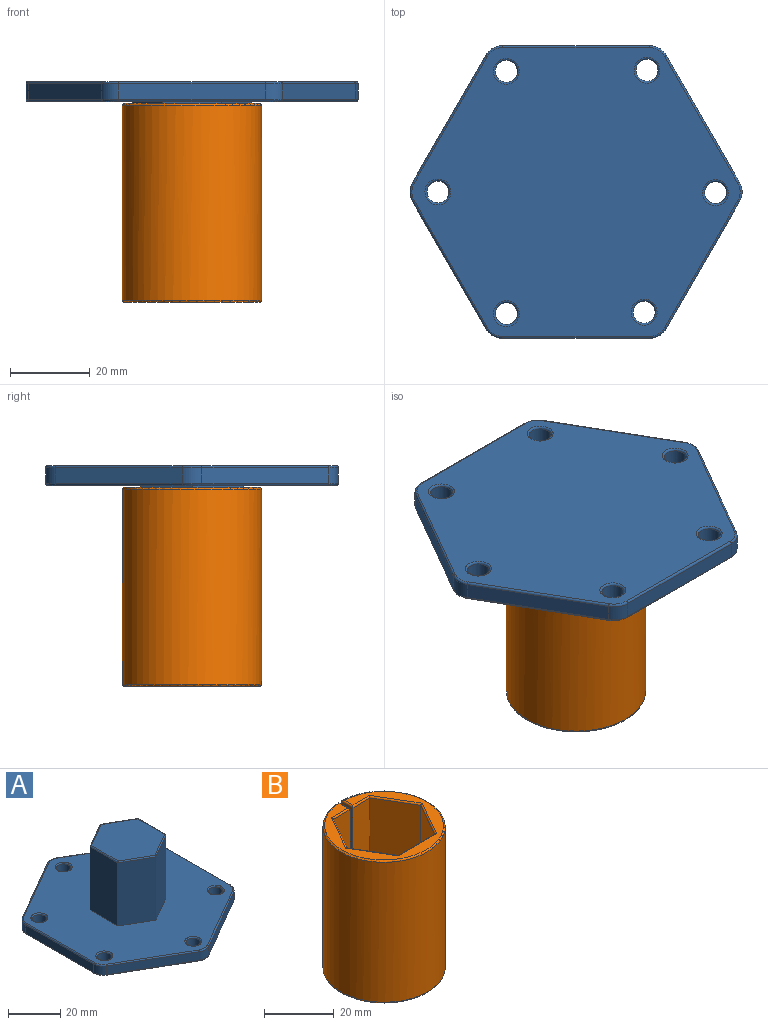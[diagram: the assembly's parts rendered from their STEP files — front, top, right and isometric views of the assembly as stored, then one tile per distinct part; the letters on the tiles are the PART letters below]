
ASSEMBLY  parts=2 mates=1
PART A: 69 faces, bbox 74.4x84.3x35 mm
  f0: plane 31.81x18.36mm, normal (0.5,0.87,0), area 146.9mm2, adj f27,f32,f33,f45
  f1: plane 31.81x18.36mm, normal (-0.5,0.87,0), area 146.9mm2, adj f27,f28,f36,f48
  f2: plane 36.73x4mm, normal (-1,0,0), area 146.9mm2, adj f28,f29,f40,f52
  f3: plane 31.81x18.36mm, normal (-0.5,-0.87,0), area 146.9mm2, adj f29,f30,f44,f56
  f4: plane 31.81x18.36mm, normal (0.5,-0.87,0), area 146.9mm2, adj f30,f31,f41,f53
  f5: cylinder r=2.75mm len=5.5mm, axis (0,0,-1), area 69.1mm2, adj f57,f63
  f6: cylinder r=2.75mm len=5.5mm, axis (0,0,-1), area 69.1mm2, adj f62,f68
  f7: cylinder r=2.75mm len=5.5mm, axis (0,0,-1), area 69.1mm2, adj f61,f67
  f8: cylinder r=2.75mm len=5.5mm, axis (0,0,-1), area 69.1mm2, adj f60,f66
  f9: cylinder r=2.75mm len=5.5mm, axis (0,0,-1), area 69.1mm2, adj f59,f65
  f10: cylinder r=2.75mm len=5.5mm, axis (0,0,-1), area 69.1mm2, adj f58,f64
  f11: plane 36.73x4mm, normal (1,0,0), area 146.9mm2, adj f31,f32,f37,f49
  f12: plane 82.45x72.61mm, normal (0,0,1), area 3775.9mm2, adj f14,f15,f16,f17,f18,f19,f33,f34
  f13: plane 82.45x72.61mm, normal (0,0,-1), area 4360.5mm2, adj f45,f46,f47,f48,f49,f50,f51,f52
  f14: plane 29.5x15mm, normal (1,0,0), area 442.5mm2, adj f12,f15,f19,f23
  f15: plane 29.5x12.99mm, normal (0.5,0.87,0), area 442.5mm2, adj f12,f14,f16,f21
  f16: plane 29.5x12.99mm, normal (-0.5,0.87,0), area 442.5mm2, adj f12,f15,f17,f22
  f17: plane 29.5x15mm, normal (-1,0,0), area 442.5mm2, adj f12,f16,f18,f24
  f18: plane 29.5x12.99mm, normal (-0.5,-0.87,0), area 442.5mm2, adj f12,f17,f19,f26
  f19: plane 29.5x12.99mm, normal (0.5,-0.87,0), area 442.5mm2, adj f12,f14,f18,f25
  f20: plane 28.85x24.98mm, normal (0,0,1), area 540.4mm2, adj f21,f22,f23,f24,f25,f26
  f21: cylinder r=0.5mm len=13.24mm, axis (0.87,-0.5,0), area 11.6mm2, adj f15,f20,f22,f23
  f22: cylinder r=0.5mm len=13.24mm, axis (0.87,0.5,0), area 11.6mm2, adj f16,f20,f21,f24
  f23: cylinder r=0.5mm len=15mm, axis (0,-1,0), area 11.6mm2, adj f14,f20,f21,f25
  f24: cylinder r=0.5mm len=15mm, axis (0,1,0), area 11.6mm2, adj f17,f20,f22,f26
  f25: cylinder r=0.5mm len=13.24mm, axis (-0.87,-0.5,0), area 11.6mm2, adj f19,f20,f23,f26
  f26: cylinder r=0.5mm len=13.24mm, axis (-0.87,0.5,0), area 11.6mm2, adj f18,f20,f24,f25
  f27: cylinder r=5mm len=5mm, axis (0,0,-1), area 20.9mm2, adj f0,f1,f34,f46
  f28: cylinder r=5mm len=4.33mm, axis (0,0,-1), area 20.9mm2, adj f1,f2,f38,f50
  f29: cylinder r=5mm len=4.33mm, axis (0,0,-1), area 20.9mm2, adj f2,f3,f42,f54
  f30: cylinder r=5mm len=5mm, axis (0,0,-1), area 20.9mm2, adj f3,f4,f43,f55
  f31: cylinder r=5mm len=4.33mm, axis (0,0,-1), area 20.9mm2, adj f4,f11,f39,f51
  f32: cylinder r=5mm len=4.33mm, axis (0,0,-1), area 20.9mm2, adj f0,f11,f35,f47
  f33: cylinder r=0.5mm len=32.06mm, axis (0.87,-0.5,0), area 28.8mm2, adj f0,f12,f34,f35
  f34: torus R=4.5mm, axis (0,0,1), area 4mm2, adj f12,f27,f33,f36
  f35: torus R=4.5mm, axis (0,0,1), area 4mm2, adj f12,f32,f33,f37
  f36: cylinder r=0.5mm len=32.06mm, axis (0.87,0.5,0), area 28.8mm2, adj f1,f12,f34,f38
  f37: cylinder r=0.5mm len=36.73mm, axis (0,-1,0), area 28.8mm2, adj f11,f12,f35,f39
  f38: torus R=4.5mm, axis (0,0,1), area 4mm2, adj f12,f28,f36,f40
  f39: torus R=4.5mm, axis (0,0,1), area 4mm2, adj f12,f31,f37,f41
  f40: cylinder r=0.5mm len=36.73mm, axis (0,1,0), area 28.8mm2, adj f2,f12,f38,f42
  f41: cylinder r=0.5mm len=32.06mm, axis (-0.87,-0.5,0), area 28.8mm2, adj f4,f12,f39,f43
  f42: torus R=4.5mm, axis (0,0,1), area 4mm2, adj f12,f29,f40,f44
  f43: torus R=4.5mm, axis (0,0,1), area 4mm2, adj f12,f30,f41,f44
  f44: cylinder r=0.5mm len=32.06mm, axis (-0.87,0.5,0), area 28.8mm2, adj f3,f12,f42,f43
  f45: cylinder r=0.5mm len=32.06mm, axis (-0.87,0.5,0), area 28.8mm2, adj f0,f13,f46,f47
  f46: torus R=4.5mm, axis (0,0,1), area 4mm2, adj f13,f27,f45,f48
  f47: torus R=4.5mm, axis (0,0,1), area 4mm2, adj f13,f32,f45,f49
  f48: cylinder r=0.5mm len=32.06mm, axis (-0.87,-0.5,0), area 28.8mm2, adj f1,f13,f46,f50
  f49: cylinder r=0.5mm len=36.73mm, axis (0,1,0), area 28.8mm2, adj f11,f13,f47,f51
  f50: torus R=4.5mm, axis (0,0,1), area 4mm2, adj f13,f28,f48,f52
  f51: torus R=4.5mm, axis (0,0,1), area 4mm2, adj f13,f31,f49,f53
  f52: cylinder r=0.5mm len=36.73mm, axis (0,-1,0), area 28.8mm2, adj f2,f13,f50,f54
  f53: cylinder r=0.5mm len=32.06mm, axis (0.87,0.5,0), area 28.8mm2, adj f4,f13,f51,f55
  f54: torus R=4.5mm, axis (0,0,1), area 4mm2, adj f13,f29,f52,f56
  f55: torus R=4.5mm, axis (0,0,1), area 4mm2, adj f13,f30,f53,f56
  f56: cylinder r=0.5mm len=32.06mm, axis (0.87,-0.5,0), area 28.8mm2, adj f3,f13,f54,f55
  f57: torus R=3.25mm, axis (0,0,1), area 14.5mm2, adj f5,f13
  f58: torus R=3.25mm, axis (0,0,1), area 14.5mm2, adj f10,f13
  f59: torus R=3.25mm, axis (0,0,1), area 14.5mm2, adj f9,f13
  f60: torus R=3.25mm, axis (0,0,1), area 14.5mm2, adj f8,f13
  f61: torus R=3.25mm, axis (0,0,1), area 14.5mm2, adj f7,f13
  f62: torus R=3.25mm, axis (0,0,1), area 14.5mm2, adj f6,f13
  f63: torus R=3.25mm, axis (0,0,1), area 14.5mm2, adj f5,f12
  f64: torus R=3.25mm, axis (0,0,1), area 14.5mm2, adj f10,f12
  f65: torus R=3.25mm, axis (0,0,1), area 14.5mm2, adj f9,f12
  f66: torus R=3.25mm, axis (0,0,1), area 14.5mm2, adj f8,f12
  f67: torus R=3.25mm, axis (0,0,1), area 14.5mm2, adj f7,f12
  f68: torus R=3.25mm, axis (0,0,1), area 14.5mm2, adj f6,f12
PART B: 33 faces, bbox 37.9x37.9x50 mm
  f0: cylinder r=4.5mm len=9mm, axis (0,0,-1), area 127.2mm2, adj f24,f31
  f1: plane 34x33.98mm, normal (0,0,1), area 269.8mm2, adj f14,f15,f16,f17,f18,f19,f20,f21
  f2: cylinder r=17.5mm len=49mm, axis (0,0,-1), area 5360.1mm2, adj f11,f12,f13,f19,f32
  f3: plane 34x34mm, normal (0,0,-1), area 829.4mm2, adj f31,f32
  f4: plane 29.5x12.91mm, normal (-0.86,-0.51,0), area 442.5mm2, adj f5,f9,f10,f14
  f5: plane 29.5x13.07mm, normal (-0.87,0.49,0), area 442.5mm2, adj f4,f6,f10,f16
  f6: plane 29.5x15mm, normal (-0.01,1,0), area 442.5mm2, adj f5,f7,f10,f18
  f7: plane 29.5x12.91mm, normal (0.86,0.51,0), area 442.5mm2, adj f6,f8,f10,f20
  f8: plane 29.5x13.07mm, normal (0.87,-0.49,0), area 442.5mm2, adj f7,f9,f10,f22
  f9: plane 29.5x15mm, normal (0.01,-1,0), area 414.8mm2, adj f4,f8,f10,f11,f12,f13,f15,f23
  f10: plane 30x26.15mm, normal (0,0,1), area 438.4mm2, adj f4,f5,f6,f7,f8,f9,f25,f26
  f11: plane 4.52x1.23mm, normal (0,0,1), area 5.3mm2, adj f2,f9,f12,f13
  f12: plane 23.43x4.5mm, normal (1,0.01,0), area 105.4mm2, adj f2,f9,f11,f21
  f13: plane 23.43x4.5mm, normal (-1,-0.01,0), area 105.4mm2, adj f2,f9,f11,f17
  f14: cylinder r=0.5mm len=13.66mm, axis (-0.51,0.86,0), area 11.9mm2, adj f1,f4,f15,f16
  f15: cylinder r=0.5mm len=7.2mm, axis (-1,-0.01,0), area 5.4mm2, adj f1,f9,f14,f17
  f16: cylinder r=0.5mm len=13.82mm, axis (0.49,0.87,0), area 11.9mm2, adj f1,f5,f14,f18
  f17: cylinder r=0.5mm len=4.51mm, axis (0.01,-1,0), area 3.2mm2, adj f1,f13,f15,f19
  f18: cylinder r=0.5mm len=15.58mm, axis (1,0.01,0), area 11.9mm2, adj f1,f6,f16,f20
  f19: torus R=17mm, axis (0,0,1), area 84.2mm2, adj f1,f2,f17,f21
  f20: cylinder r=0.5mm len=13.66mm, axis (0.51,-0.86,0), area 11.9mm2, adj f1,f7,f18,f22
  f21: cylinder r=0.5mm len=4.51mm, axis (-0.01,1,0), area 3.2mm2, adj f1,f12,f19,f23
  f22: cylinder r=0.5mm len=13.82mm, axis (-0.49,-0.87,0), area 11.9mm2, adj f1,f8,f20,f23
  f23: cylinder r=0.5mm len=7.2mm, axis (-1,-0.01,0), area 5.4mm2, adj f1,f9,f21,f22
  f24: plane 15x13.03mm, normal (0,0,1), area 82.5mm2, adj f0,f25,f26,f27,f28,f29,f30
  f25: plane 15x7.5mm, normal (0.01,-1,0), area 112.5mm2, adj f10,f24,f26,f30
  f26: plane 15x6.52mm, normal (0.87,-0.49,0), area 112.5mm2, adj f10,f24,f25,f27
  f27: plane 15x6.47mm, normal (0.86,0.51,0), area 112.5mm2, adj f10,f24,f26,f28
  f28: plane 15x7.5mm, normal (-0.01,1,0), area 112.5mm2, adj f10,f24,f27,f29
  f29: plane 15x6.52mm, normal (-0.87,0.49,0), area 112.5mm2, adj f10,f24,f28,f30
  f30: plane 15x6.47mm, normal (-0.86,-0.51,0), area 112.5mm2, adj f10,f24,f25,f29
  f31: torus R=5mm, axis (0,0,1), area 23.1mm2, adj f0,f3
  f32: torus R=17mm, axis (0,0,1), area 85.5mm2, adj f2,f3
PLACE A rot(axis=(-0.71,0.71,0),180deg) t=(0,0,35.48)mm
PLACE B t=(0,0,-20)mm
MATE slider A.f20 <-> B.f0  axis (0,0,-1) through (0,0,0.48)mm
